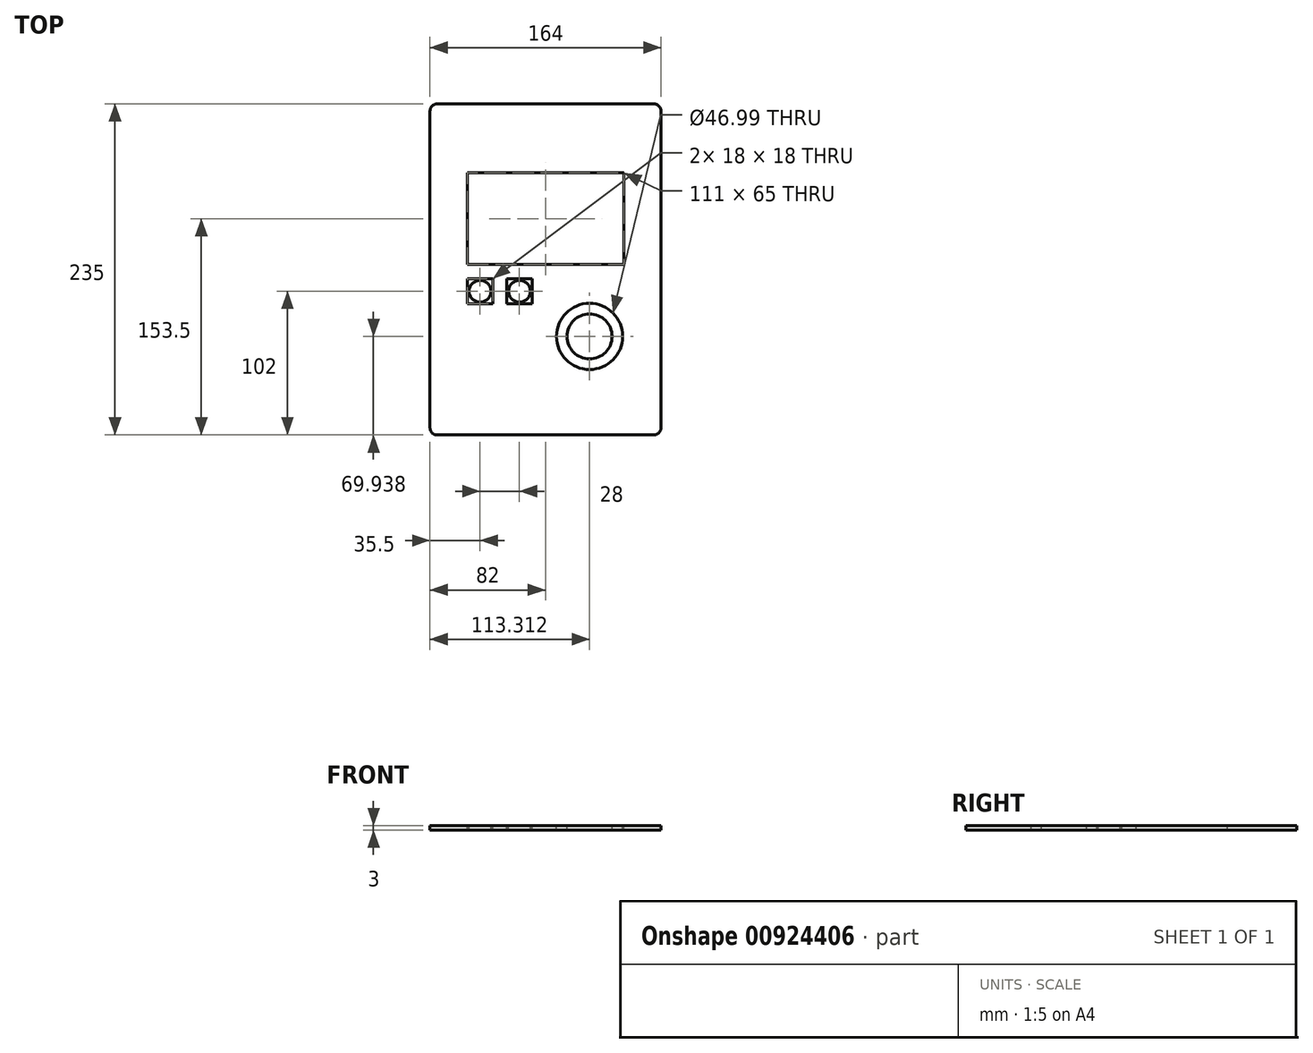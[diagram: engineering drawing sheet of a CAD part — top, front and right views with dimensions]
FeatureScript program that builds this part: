
annotation { "Feature Type Name" : "Feature", "Feature Type Description" : "" }
export const myFeature = defineFeature(function(context is Context, id is Id, definition is map)
    precondition{}
    {
        {
            var Q0;
            Q0=qCreatedBy(makeId("Top.planeOp"),FACE);
            var sketch = newSketch(context, id + "F0", { "sketchPlane" : qUnion([Q0])});
            skLineSegment(sketch, "E0.bottom", {"start": v(0, 0) * mm, "end": v(154, 0) * mm, "construction": true});
            skLineSegment(sketch, "E0.top", {"start": v(0, 225) * mm, "end": v(154, 225) * mm, "construction": true});
            skLineSegment(sketch, "E0.left", {"start": v(0, 0) * mm, "end": v(0, 225) * mm, "construction": true});
            skLineSegment(sketch, "E0.right", {"start": v(154, 0) * mm, "end": v(154, 225) * mm, "construction": true});
            skLineSegment(sketch, "E1.bottom", {"start": v(25.5, 177) * mm, "end": v(128.5, 177) * mm});
            skLineSegment(sketch, "E1.top", {"start": v(25.5, 120) * mm, "end": v(128.5, 120) * mm});
            skLineSegment(sketch, "E1.left", {"start": v(25.5, 177) * mm, "end": v(25.5, 120) * mm});
            skLineSegment(sketch, "E1.right", {"start": v(128.5, 177) * mm, "end": v(128.5, 120) * mm});
            skLineSegment(sketch, "E2", {"start": v(77, 0) * mm, "end": v(77, 225) * mm, "construction": true});
            skLineSegment(sketch, "E3", {"start": v(0, 112.5) * mm, "end": v(154, 112.5) * mm, "construction": true});
            skLineSegment(sketch, "E4.bottom", {"start": v(-5, 230) * mm, "end": v(159, 230) * mm});
            skLineSegment(sketch, "E4.top", {"start": v(-5, -5) * mm, "end": v(159, -5) * mm});
            skLineSegment(sketch, "E4.left", {"start": v(-5, 230) * mm, "end": v(-5, -5) * mm});
            skLineSegment(sketch, "E4.right", {"start": v(159, 230) * mm, "end": v(159, -5) * mm});
            skSolve(sketch);
        }
        {
            var Q0;
            Q0=qSketchRegion(id+"F0",true);
            extrude(context, id + "F1", {"entities" : qUnion([Q0]), "depth" : 3 * mm, "offsetDistance" : 25 * mm});
        }
        {
            var Q0;
            Q0=makeQuery(id+"F1.opExtrude","SWEPT_EDGE",EDGE,{"disambiguationData":[OSD([sQuery(id+"F0.wireOp",EDGE,"E4.bottom"),sQuery(id+"F0.wireOp",EDGE,"E4.left")])]});
            var Q1;
            Q1=makeQuery(id+"F1.opExtrude","SWEPT_EDGE",EDGE,{"disambiguationData":[OSD([sQuery(id+"F0.wireOp",EDGE,"E4.bottom"),sQuery(id+"F0.wireOp",EDGE,"E4.right")])]});
            var Q2;
            Q2=makeQuery(id+"F1.opExtrude","SWEPT_EDGE",EDGE,{"disambiguationData":[OSD([sQuery(id+"F0.wireOp",EDGE,"E4.top"),sQuery(id+"F0.wireOp",EDGE,"E4.right")])]});
            var Q3;
            Q3=makeQuery(id+"F1.opExtrude","SWEPT_EDGE",EDGE,{"disambiguationData":[OSD([sQuery(id+"F0.wireOp",EDGE,"E4.top"),sQuery(id+"F0.wireOp",EDGE,"E4.left")])]});
            fillet(context, id + "F2", {"entities" : qUnion([Q0, Q1, Q2, Q3]), "radius" : 5 * mm, "tangentPropagation" : true, "allowEdgeOverflow" : false});
        }
        {
            var Q0;
            Q0=makeQuery(id+"F1.opExtrude","CAP_FACE",FACE,{"disambiguationData":[OSD([sQuery(id+"F0.wireOp",EDGE,"E1.bottom"),sQuery(id+"F0.wireOp",EDGE,"E1.top"),sQuery(id+"F0.wireOp",EDGE,"E1.left"),sQuery(id+"F0.wireOp",EDGE,"E1.right"),sQuery(id+"F0.wireOp",EDGE,"E4.bottom"),sQuery(id+"F0.wireOp",EDGE,"E4.top"),sQuery(id+"F0.wireOp",EDGE,"E4.left"),sQuery(id+"F0.wireOp",EDGE,"E4.right")])],"isStart":false});
            var sketch = newSketch(context, id + "F3", { "sketchPlane" : qUnion([Q0])});
            skCircle(sketch, "E5", {"center": v(30.5, 97) * mm, "radius": 7.75 * mm});
            skLineSegment(sketch, "E6.bottom", {"start": v(39.5, 88) * mm, "end": v(21.5, 88) * mm});
            skLineSegment(sketch, "E6.top", {"start": v(39.5, 106) * mm, "end": v(21.5, 106) * mm});
            skLineSegment(sketch, "E6.left", {"start": v(39.5, 88) * mm, "end": v(39.5, 106) * mm});
            skLineSegment(sketch, "E6.right", {"start": v(21.5, 88) * mm, "end": v(21.5, 106) * mm});
            skLineSegment(sketch, "E7", {"start": v(39.5, 106) * mm, "end": v(21.5, 88) * mm});
            skLineSegment(sketch, "E8", {"start": v(21.5, 106) * mm, "end": v(39.5, 88) * mm});
            skLineSegment(sketch, "E9.bottom", {"start": v(132.5, 116) * mm, "end": v(21.5, 116) * mm});
            skLineSegment(sketch, "E9.top", {"start": v(132.5, 181) * mm, "end": v(21.5, 181) * mm});
            skLineSegment(sketch, "E9.left", {"start": v(132.5, 116) * mm, "end": v(132.5, 181) * mm});
            skLineSegment(sketch, "E9.right", {"start": v(21.5, 116) * mm, "end": v(21.5, 181) * mm});
            skPoint(sketch, "E9.middle", {"position": v(77, 148.5) * mm});
            skLineSegment(sketch, "E10", {"start": v(77, 181) * mm, "end": v(77, 116) * mm, "construction": true});
            skLineSegment(sketch, "E11", {"start": v(132.5, 148.5) * mm, "end": v(21.5, 148.5) * mm, "construction": true});
            skLineSegment(sketch, "E12.1.0.0", {"start": v(67.5, 88) * mm, "end": v(49.5, 88) * mm});
            skLineSegment(sketch, "E12.1.0.1", {"start": v(67.5, 106) * mm, "end": v(49.5, 106) * mm});
            skLineSegment(sketch, "E12.1.0.2", {"start": v(67.5, 88) * mm, "end": v(67.5, 106) * mm});
            skLineSegment(sketch, "E12.1.0.3", {"start": v(49.5, 88) * mm, "end": v(49.5, 106) * mm});
            skLineSegment(sketch, "E12.1.0.4", {"start": v(67.5, 106) * mm, "end": v(49.5, 88) * mm});
            skLineSegment(sketch, "E12.1.0.5", {"start": v(49.5, 106) * mm, "end": v(67.5, 88) * mm});
            skPoint(sketch, "E12.1.0.6", {"position": v(58.5, 97) * mm});
            skCircle(sketch, "E12.1.0.7", {"center": v(58.5, 97) * mm, "radius": 7.75 * mm});
            skLineSegment(sketch, "E12.direction1", {"start": v(21.5, 88) * mm, "end": v(49.5, 88) * mm});
            skCircle(sketch, "E13", {"center": v(108.31, 64.94) * mm, "radius": 4.6 * mm});
            skCircle(sketch, "E14", {"center": v(108.31, 64.94) * mm, "radius": 9.5 * mm});
            skCircle(sketch, "E15", {"center": v(108.31, 64.94) * mm, "radius": 16 * mm});
            skCircle(sketch, "E16", {"center": v(98.71, 61.8) * mm, "radius": 1.5 * mm});
            skLineSegment(sketch, "E17", {"start": v(108.31, 64.94) * mm, "end": v(113.3, 87.9) * mm});
            skLineSegment(sketch, "E18", {"start": v(108.31, 64.94) * mm, "end": v(119.24, 44.14) * mm});
            skLineSegment(sketch, "E19", {"start": v(108.31, 64.94) * mm, "end": v(123.5, 82.87) * mm});
            skLineSegment(sketch, "E20", {"start": v(108.31, 64.94) * mm, "end": v(130.14, 73.64) * mm});
            skLineSegment(sketch, "E21", {"start": v(108.31, 64.94) * mm, "end": v(131.67, 62.37) * mm});
            skLineSegment(sketch, "E22", {"start": v(108.31, 64.94) * mm, "end": v(127.73, 51.7) * mm});
            skCircle(sketch, "E23", {"center": v(108.31, 64.94) * mm, "radius": 23.5 * mm});
            skSolve(sketch);
        }
        {
            var Q0;
            Q0 = qSketchRegion(id + "F3", true);
            extrude(context, id + "F4", {"entities" : qUnion([Q0]), "operationType" : NewBodyOperationType.REMOVE, "endBound" : BoundingType.THROUGH_ALL, "oppositeDirection" : true, "depth" : 25 * mm, "offsetDistance" : 25 * mm});
        }
    });
